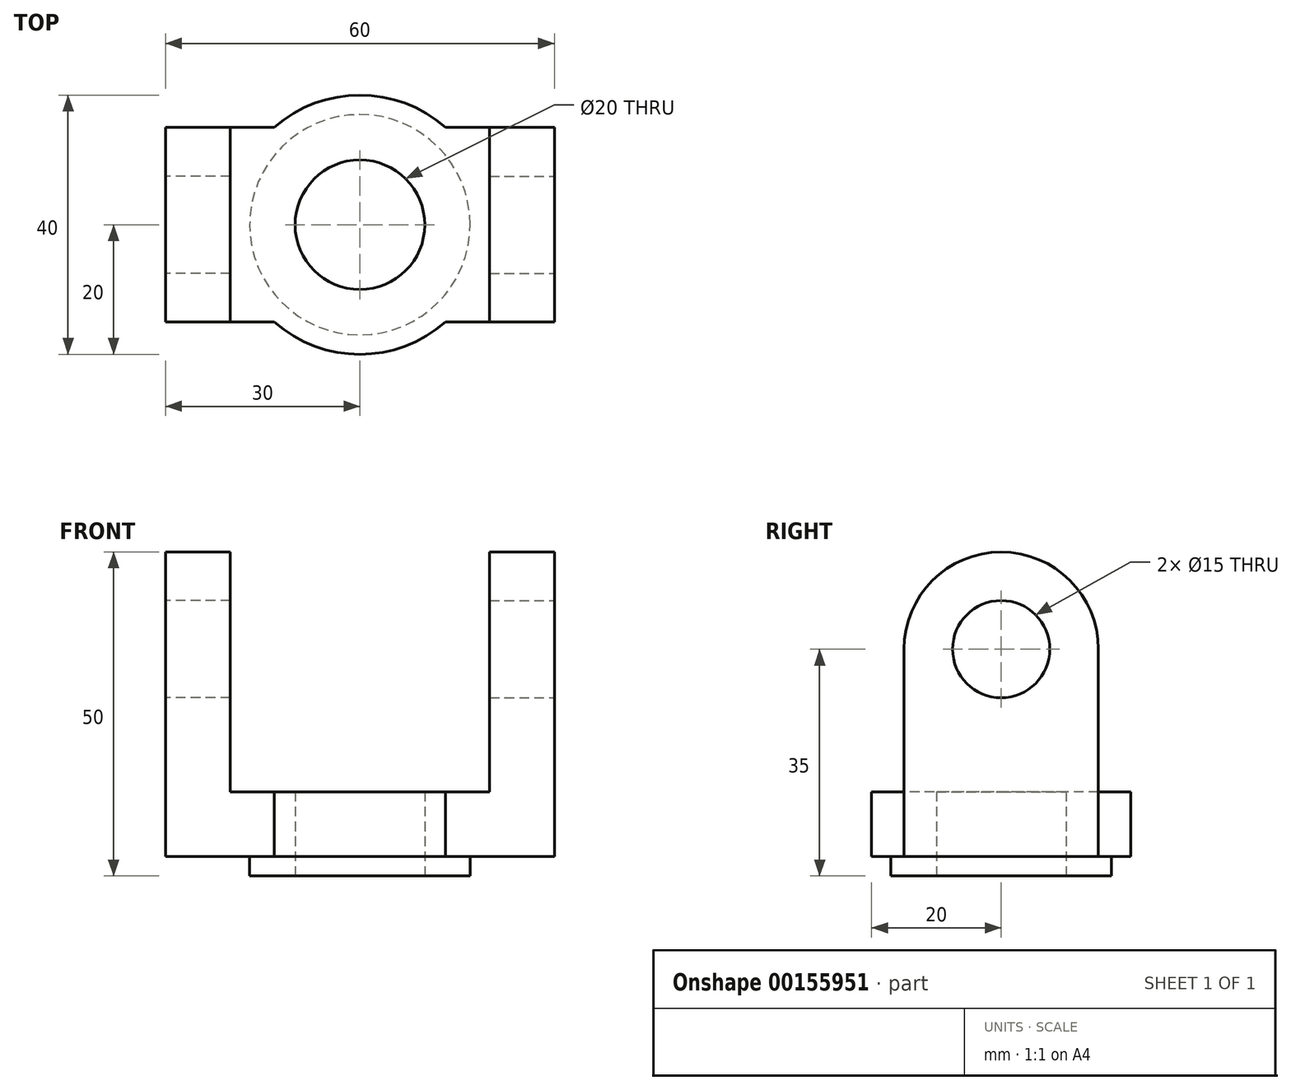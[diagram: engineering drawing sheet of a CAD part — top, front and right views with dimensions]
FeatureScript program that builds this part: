
annotation { "Feature Type Name" : "Feature", "Feature Type Description" : "" }
export const myFeature = defineFeature(function(context is Context, id is Id, definition is map)
    precondition{}
    {
        {
            var Q0;
            Q0=qCreatedBy(makeId("Top.planeOp"),FACE);
            var sketch = newSketch(context, id + "F0", { "sketchPlane" : qUnion([Q0])});
            skLineSegment(sketch, "E0.bottom", {"start": v(30, 15) * mm, "end": v(-30, 15) * mm});
            skLineSegment(sketch, "E0.top", {"start": v(30, -15) * mm, "end": v(-30, -15) * mm});
            skLineSegment(sketch, "E0.left", {"start": v(30, 15) * mm, "end": v(30, -15) * mm});
            skLineSegment(sketch, "E0.right", {"start": v(-30, 15) * mm, "end": v(-30, -15) * mm});
            skPoint(sketch, "E0.middle", {"position": v(0, 0) * mm});
            skCircle(sketch, "E1", {"center": v(0, 0) * mm, "radius": 20 * mm});
            skCircle(sketch, "E2", {"center": v(0, 0) * mm, "radius": 10 * mm});
            skSolve(sketch);
        }
        {
            var Q0;
            {var subQ0=sQuery(id+"F0.wireOp",EDGE,"E0.right");Q0=makeQuery(id+"F0.imprint","IMPRINT",FACE,{"disambiguationData":[TD([[makeQuery(id+"F0.imprint","IMPRINT",EDGE,{"derivedFrom":subQ0}),1.0]])]});}
            var Q1;
            {var subQ0=sQuery(id+"F0.wireOp",EDGE,"E1");var subQ1=sQuery(id+"F0.wireOp",EDGE,"E0.bottom");var subQ2=makeQuery(id+"F0.imprint","INTERSECT",VERTEX,{"disambiguationData":[OD(0.0)],"derivedFrom":[subQ1,subQ0]});Q1=makeQuery(id+"F0.imprint","IMPRINT",FACE,{"disambiguationData":[TD([[makeQuery(id+"F0.imprint","IMPRINT",EDGE,{"disambiguationData":[TD([[subQ2,-1.0]])],"derivedFrom":subQ1}),-1.0]])]});}
            var Q2;
            Q2=makeQuery(id+"F0.imprint","IMPRINT",FACE,{"disambiguationData":[TD([[makeQuery(id+"F0.imprint","IMPRINT",EDGE,{"derivedFrom":sQuery(id+"F0.wireOp",EDGE,"E2")}),-1.0]])]});
            var Q3;
            {var subQ0=sQuery(id+"F0.wireOp",EDGE,"E0.left");Q3=makeQuery(id+"F0.imprint","IMPRINT",FACE,{"disambiguationData":[TD([[makeQuery(id+"F0.imprint","IMPRINT",EDGE,{"derivedFrom":subQ0}),-1.0]])]});}
            var Q4;
            {var subQ0=sQuery(id+"F0.wireOp",EDGE,"E1");var subQ1=sQuery(id+"F0.wireOp",EDGE,"E0.top");var subQ2=makeQuery(id+"F0.imprint","INTERSECT",VERTEX,{"disambiguationData":[OD(0.0)],"derivedFrom":[subQ1,subQ0]});Q4=makeQuery(id+"F0.imprint","IMPRINT",FACE,{"disambiguationData":[TD([[makeQuery(id+"F0.imprint","IMPRINT",EDGE,{"disambiguationData":[TD([[subQ2,-1.0]])],"derivedFrom":subQ1}),1.0]])]});}
            extrude(context, id + "F1", {"entities" : qUnion([Q0, Q1, Q2, Q3, Q4]), "depth" : 10 * mm});
        }
        {
            var Q0;
            Q0=makeQuery(id+"F1.opExtrude","CAP_FACE",FACE,{"disambiguationData":[OSD([sQuery(id+"F0.wireOp",EDGE,"E0.bottom"),sQuery(id+"F0.wireOp",EDGE,"E0.top"),sQuery(id+"F0.wireOp",EDGE,"E0.left"),sQuery(id+"F0.wireOp",EDGE,"E0.right"),sQuery(id+"F0.wireOp",EDGE,"E1"),sQuery(id+"F0.wireOp",EDGE,"E2")])],"isStart":true});
            var sketch = newSketch(context, id + "F2", { "sketchPlane" : qUnion([Q0])});
            skCircle(sketch, "E3", {"center": v(0, 0) * mm, "radius": 17 * mm});
            skSolve(sketch);
        }
        {
            var Q0;
            Q0=makeQuery(id+"F2.imprint","IMPRINT",FACE,{"disambiguationData":[TD([[makeQuery(id+"F2.imprint","IMPRINT",EDGE,{"derivedFrom":sQuery(id+"F2.wireOp",EDGE,"E3")}),1.0]])]});
            extrude(context, id + "F3", {"entities" : qUnion([Q0]), "operationType" : NewBodyOperationType.ADD, "depth" : 3 * mm});
        }
        {
            var Q0;
            Q0=makeQuery(id+"F1.opExtrude","SWEPT_FACE",FACE,{"disambiguationData":[OSD([sQuery(id+"F0.wireOp",EDGE,"E0.left")])]});
            var sketch = newSketch(context, id + "F4", { "sketchPlane" : qUnion([Q0])});
            skCircle(sketch, "E4", {"center": v(0, 32) * mm, "radius": 7.5 * mm});
            skPoint(sketch, "E4.centerSnap0", {"position": v(0, 0) * mm});
            skLineSegment(sketch, "E5.bottom", {"start": v(-15, 10) * mm, "end": v(15, 10) * mm});
            skLineSegment(sketch, "E5.left", {"start": v(-15, 10) * mm, "end": v(-15, 32) * mm});
            skLineSegment(sketch, "E5.right", {"start": v(15, 10) * mm, "end": v(15, 32) * mm});
            skArc(sketch, "E6", {"start": v(-15, 32) * mm, "mid": v(0, 47) * mm, "end": v(15, 32) * mm});
            skSolve(sketch);
        }
        {
            var Q0;
            Q0=makeQuery(id+"F4.imprint","IMPRINT",FACE,{"disambiguationData":[TD([[makeQuery(id+"F4.imprint","IMPRINT",EDGE,{"derivedFrom":sQuery(id+"F4.wireOp",EDGE,"E4")}),-1.0]])]});
            extrude(context, id + "F5", {"entities" : qUnion([Q0]), "operationType" : NewBodyOperationType.ADD, "oppositeDirection" : true, "depth" : 10 * mm});
        }
        {
            var Q0;
            Q0=makeQuery(id+"F1.opExtrude","SWEPT_FACE",FACE,{"disambiguationData":[OSD([sQuery(id+"F0.wireOp",EDGE,"E0.right")])]});
            var sketch = newSketch(context, id + "F6", { "sketchPlane" : qUnion([Q0])});
            skLineSegment(sketch, "E7.0.0", {"start": v(15, 10) * mm, "end": v(15, 32) * mm});
            skArc(sketch, "E7.0.1", {"start": v(15, 32) * mm, "mid": v(0, 47) * mm, "end": v(-15, 32) * mm});
            skLineSegment(sketch, "E7.0.2", {"start": v(-15, 32) * mm, "end": v(-15, 10) * mm});
            skLineSegment(sketch, "E7.0.3", {"start": v(-15, 10) * mm, "end": v(15, 10) * mm});
            skCircle(sketch, "E8.0", {"center": v(0, 32) * mm, "radius": 7.5 * mm});
            skSolve(sketch);
        }
        {
            var Q0;
            Q0=makeQuery(id+"F6.imprint","IMPRINT",FACE,{"disambiguationData":[TD([[makeQuery(id+"F6.imprint","IMPRINT",EDGE,{"derivedFrom":sQuery(id+"F6.wireOp",EDGE,"E7.0.0")}),1.0]])]});
            extrude(context, id + "F7", {"entities" : qUnion([Q0]), "operationType" : NewBodyOperationType.ADD, "oppositeDirection" : true, "depth" : 10 * mm});
        }
    });
